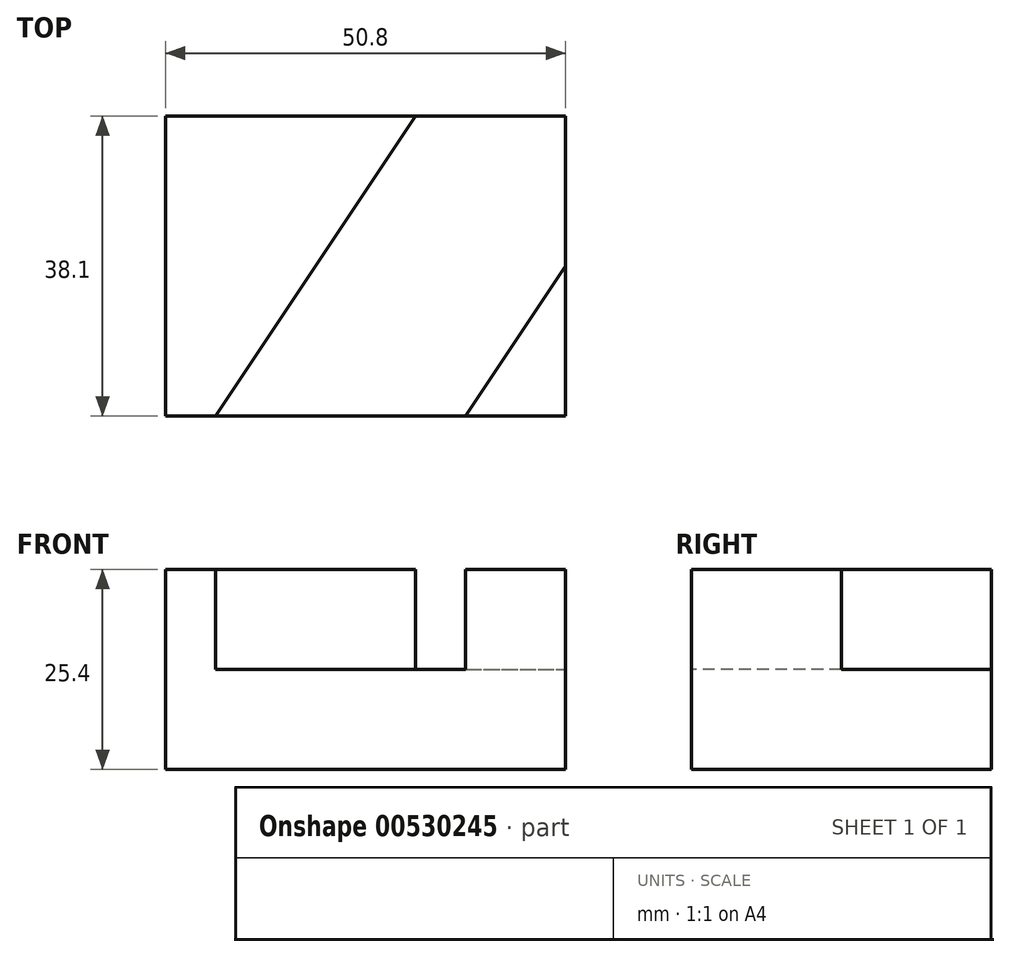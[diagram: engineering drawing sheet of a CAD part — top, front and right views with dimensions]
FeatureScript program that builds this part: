
annotation { "Feature Type Name" : "Feature", "Feature Type Description" : "" }
export const myFeature = defineFeature(function(context is Context, id is Id, definition is map)
    precondition{}
    {
        {
            var Q0;
            Q0=qCreatedBy(makeId("Top.planeOp"),FACE);
            var sketch = newSketch(context, id + "F0", { "sketchPlane" : qUnion([Q0])});
            skLineSegment(sketch, "E0", {"start": v(-61.34, 0) * mm, "end": v(-61.34, 38.1) * mm});
            skLineSegment(sketch, "E1", {"start": v(-61.34, 38.1) * mm, "end": v(-10.54, 38.1) * mm});
            skLineSegment(sketch, "E2", {"start": v(-10.54, 38.1) * mm, "end": v(-10.54, 0) * mm});
            skLineSegment(sketch, "E3", {"start": v(-10.54, 0) * mm, "end": v(-61.34, 0) * mm});
            skSolve(sketch);
        }
        {
            var Q0;
            Q0 = qSketchRegion(id + "F0", true);
            extrude(context, id + "F1", {"entities" : qUnion([Q0]), "depth" : 25.4 * mm, "offsetDistance" : 25.4 * mm});
        }
        {
            var Q0;
            Q0=makeQuery(id+"F1.opExtrude","CAP_FACE",FACE,{"disambiguationData":[OSD([sQuery(id+"F0.wireOp",EDGE,"E0"),sQuery(id+"F0.wireOp",EDGE,"E1"),sQuery(id+"F0.wireOp",EDGE,"E2"),sQuery(id+"F0.wireOp",EDGE,"E3")])],"isStart":false});
            var sketch = newSketch(context, id + "F2", { "sketchPlane" : qUnion([Q0])});
            skLineSegment(sketch, "E4", {"start": v(-29.59, 38.1) * mm, "end": v(-54.99, 0) * mm});
            skLineSegment(sketch, "E5", {"start": v(-54.99, 0) * mm, "end": v(-61.34, 0) * mm});
            skLineSegment(sketch, "E6", {"start": v(-61.34, 0) * mm, "end": v(-61.34, 38.1) * mm});
            skLineSegment(sketch, "E7", {"start": v(-61.34, 38.1) * mm, "end": v(-29.59, 38.1) * mm});
            skLineSegment(sketch, "E8", {"start": v(-23.24, 0) * mm, "end": v(-10.54, 19.05) * mm});
            skLineSegment(sketch, "E9", {"start": v(-10.54, 19.05) * mm, "end": v(-10.54, 0) * mm});
            skLineSegment(sketch, "E10", {"start": v(-10.54, 0) * mm, "end": v(-23.24, 0) * mm});
            skSolve(sketch);
        }
        {
            var Q0;
            {var subQ4=sQuery(id+"F2.wireOp",EDGE,"E4");Q0=makeQuery(id+"F2.imprint","IMPRINT",FACE,{"disambiguationData":[TD([[makeQuery(id+"F2.imprint","IMPRINT",EDGE,{"derivedFrom":subQ4}),1.0]])]});}
            extrude(context, id + "F3", {"entities" : qUnion([Q0]), "operationType" : NewBodyOperationType.REMOVE, "oppositeDirection" : true, "depth" : 12.7 * mm, "offsetDistance" : 25.4 * mm});
        }
    });
